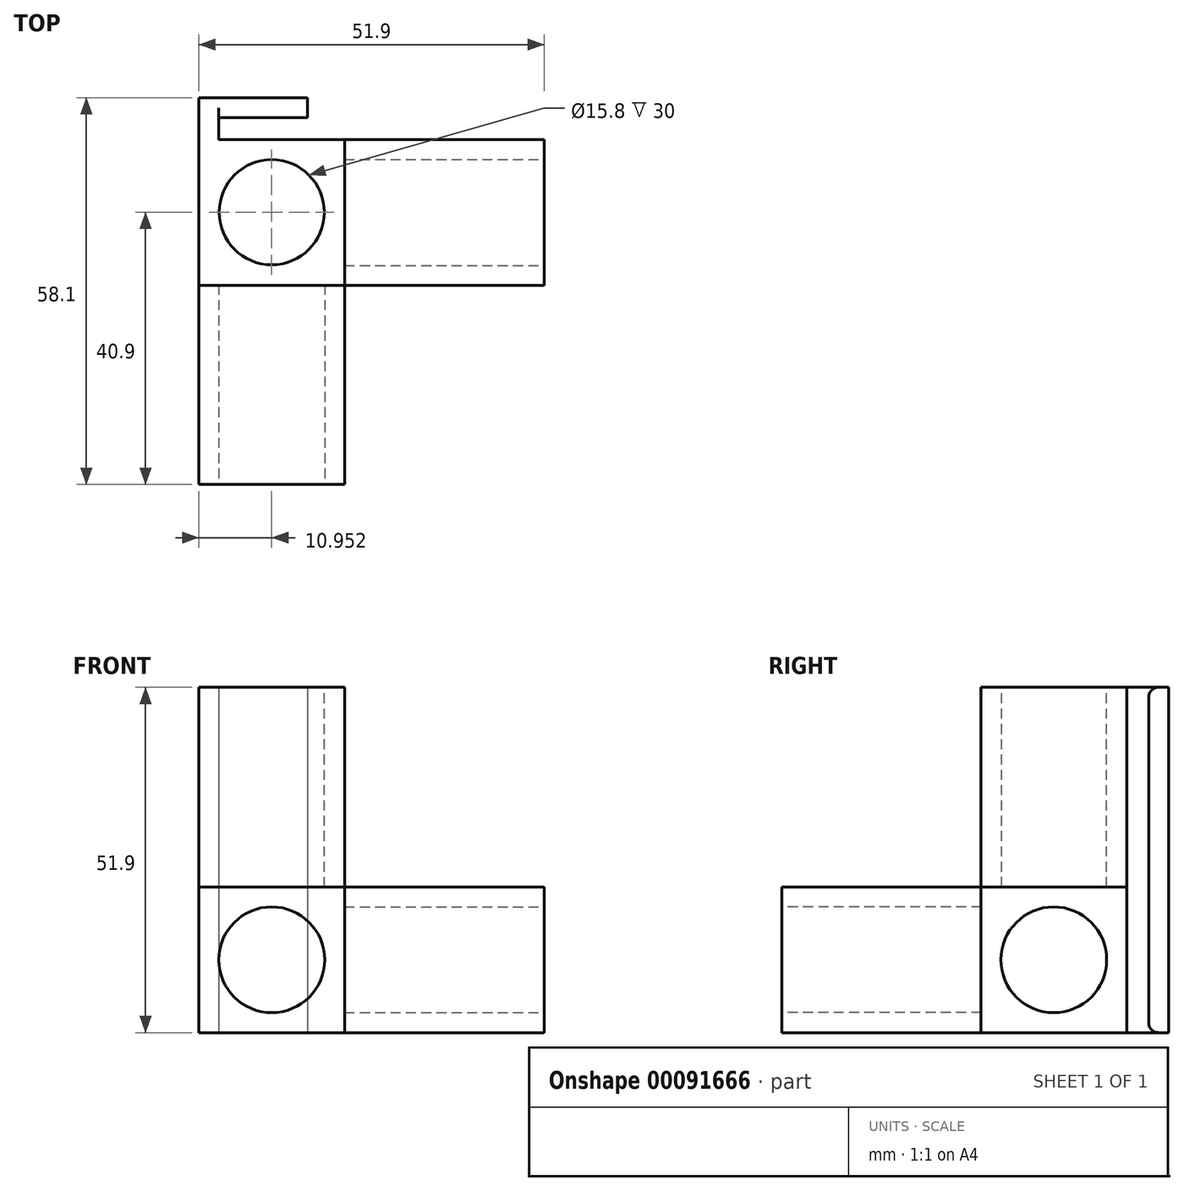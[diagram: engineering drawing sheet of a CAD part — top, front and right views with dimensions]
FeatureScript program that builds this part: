
annotation { "Feature Type Name" : "Feature", "Feature Type Description" : "" }
export const myFeature = defineFeature(function(context is Context, id is Id, definition is map)
    precondition{}
    {
        {
            var Q0;
            Q0=qCreatedBy(makeId("Front.planeOp"),FACE);
            var sketch = newSketch(context, id + "F0", { "sketchPlane" : qUnion([Q0])});
            skLineSegment(sketch, "E0.bottom", {"start": v(-42.3, 45.9) * mm, "end": v(-26.4, 45.9) * mm});
            skLineSegment(sketch, "E0.top", {"start": v(-42.3, 0) * mm, "end": v(-26.4, 0) * mm});
            skLineSegment(sketch, "E0.left", {"start": v(-42.3, 45.9) * mm, "end": v(-42.3, 0) * mm});
            skLineSegment(sketch, "E0.right", {"start": v(-26.4, 45.9) * mm, "end": v(-26.4, 15.9) * mm});
            skLineSegment(sketch, "E1.top", {"start": v(-42.3, 15.9) * mm, "end": v(-26.4, 15.9) * mm});
            skLineSegment(sketch, "E1.left", {"start": v(-42.3, 0) * mm, "end": v(-42.3, 15.9) * mm});
            skLineSegment(sketch, "E1.right", {"start": v(3.6, 0) * mm, "end": v(3.6, 15.9) * mm});
            skLineSegment(sketch, "E2", {"start": v(-26.4, 15.9) * mm, "end": v(-26.4, 0) * mm});
            skLineSegment(sketch, "E3", {"start": v(-26.4, 15.9) * mm, "end": v(3.6, 15.9) * mm});
            skLineSegment(sketch, "E4", {"start": v(-26.4, 0) * mm, "end": v(-26.4, 0) * mm});
            skLineSegment(sketch, "E5", {"start": v(-42.3, 15.9) * mm, "end": v(-42.3, 15.9) * mm});
            skLineSegment(sketch, "E6", {"start": v(-26.4, 0) * mm, "end": v(3.6, 0) * mm});
            skLineSegment(sketch, "E7.0", {"start": v(-45.3, 48.9) * mm, "end": v(-45.3, -3) * mm});
            skLineSegment(sketch, "E7.1", {"start": v(-45.3, -3) * mm, "end": v(-23.4, -3) * mm});
            skLineSegment(sketch, "E7.2", {"start": v(-23.4, 48.9) * mm, "end": v(-23.4, 18.9) * mm});
            skLineSegment(sketch, "E7.3", {"start": v(-23.4, 18.9) * mm, "end": v(6.6, 18.9) * mm});
            skLineSegment(sketch, "E7.4", {"start": v(6.6, -3) * mm, "end": v(6.6, 18.9) * mm});
            skLineSegment(sketch, "E7.5", {"start": v(-45.3, 48.9) * mm, "end": v(-23.4, 48.9) * mm});
            skLineSegment(sketch, "E7.6", {"start": v(-23.4, -3) * mm, "end": v(6.6, -3) * mm});
            skPoint(sketch, "E8", {"position": v(-34.36, 7.95) * mm});
            skPoint(sketch, "E8.positionSnap0", {"position": v(-26.4, 7.95) * mm});
            skPoint(sketch, "E8.positionSnap1", {"position": v(-34.36, 15.9) * mm});
            skCircle(sketch, "E9", {"center": v(-34.36, 7.95) * mm, "radius": 7.95 * mm});
            skLineSegment(sketch, "E10", {"start": v(-23.4, 18.9) * mm, "end": v(-45.3, 18.9) * mm});
            skLineSegment(sketch, "E11", {"start": v(-23.4, 18.9) * mm, "end": v(-23.4, -3) * mm});
            skSolve(sketch);
        }
        {
            var Q0;
            {var subQ1=sQuery(id+"F0.wireOp",EDGE,"E1.top");var subQ3=sQuery(id+"F0.wireOp",EDGE,"E9");var subQ4=makeQuery(id+"F0.imprint","INTERSECT",VERTEX,{"derivedFrom":[subQ1,subQ3]});Q0=makeQuery(id+"F0.imprint","IMPRINT",FACE,{"disambiguationData":[TD([[makeQuery(id+"F0.imprint","IMPRINT",EDGE,{"disambiguationData":[TD([[subQ4,-1.0]])],"derivedFrom":subQ3}),-1.0]])]});}
            var Q1;
            {var subQ0=sQuery(id+"F0.wireOp",EDGE,"E9");var subQ1=makeQuery(id+"F0.imprint","INTERSECT",VERTEX,{"derivedFrom":[sQuery(id+"F0.wireOp",EDGE,"E1.top"),subQ0]});Q1=makeQuery(id+"F0.imprint","IMPRINT",FACE,{"disambiguationData":[TD([[makeQuery(id+"F0.imprint","IMPRINT",EDGE,{"disambiguationData":[TD([[subQ1,1.0]])],"derivedFrom":subQ0}),1.0]])]});}
            var Q2;
            {var subQ5=sQuery(id+"F0.wireOp",EDGE,"E0.bottom");Q2=makeQuery(id+"F0.imprint","IMPRINT",FACE,{"disambiguationData":[TD([[makeQuery(id+"F0.imprint","IMPRINT",EDGE,{"derivedFrom":subQ5}),1.0]])]});}
            var Q3;
            {var subQ0=sQuery(id+"F0.wireOp",EDGE,"E1.right");Q3=makeQuery(id+"F0.imprint","IMPRINT",FACE,{"disambiguationData":[TD([[makeQuery(id+"F0.imprint","IMPRINT",EDGE,{"derivedFrom":subQ0}),1.0]])]});}
            var Q4;
            {var subQ0=sQuery(id+"F0.wireOp",EDGE,"E0.bottom");Q4=makeQuery(id+"F0.imprint","IMPRINT",FACE,{"disambiguationData":[TD([[makeQuery(id+"F0.imprint","IMPRINT",EDGE,{"derivedFrom":subQ0}),-1.0]])]});}
            var Q5;
            {var subQ0=sQuery(id+"F0.wireOp",EDGE,"E1.left");var subQ1=sQuery(id+"F0.wireOp",EDGE,"E0.top");var subQ2=makeQuery(id+"F0.imprint","INTERSECT",VERTEX,{"derivedFrom":[subQ1,subQ0]});Q5=makeQuery(id+"F0.imprint","IMPRINT",FACE,{"disambiguationData":[TD([[makeQuery(id+"F0.imprint","IMPRINT",EDGE,{"disambiguationData":[TD([[subQ2,-1.0]])],"derivedFrom":subQ1}),1.0]])]});}
            var Q6;
            {var subQ1=sQuery(id+"F0.wireOp",EDGE,"E0.top");var subQ3=sQuery(id+"F0.wireOp",EDGE,"E9");var subQ4=makeQuery(id+"F0.imprint","INTERSECT",VERTEX,{"derivedFrom":[subQ1,subQ3]});Q6=makeQuery(id+"F0.imprint","IMPRINT",FACE,{"disambiguationData":[TD([[makeQuery(id+"F0.imprint","IMPRINT",EDGE,{"disambiguationData":[TD([[subQ4,-1.0]])],"derivedFrom":subQ3}),-1.0]])]});}
            var Q7;
            {var subQ1=sQuery(id+"F0.wireOp",EDGE,"E1.top");var subQ3=sQuery(id+"F0.wireOp",EDGE,"E9");var subQ4=makeQuery(id+"F0.imprint","INTERSECT",VERTEX,{"derivedFrom":[subQ1,subQ3]});Q7=makeQuery(id+"F0.imprint","IMPRINT",FACE,{"disambiguationData":[TD([[makeQuery(id+"F0.imprint","IMPRINT",EDGE,{"disambiguationData":[TD([[subQ4,1.0]])],"derivedFrom":subQ3}),-1.0]])]});}
            var Q8;
            {var subQ5=sQuery(id+"F0.wireOp",EDGE,"E1.right");Q8=makeQuery(id+"F0.imprint","IMPRINT",FACE,{"disambiguationData":[TD([[makeQuery(id+"F0.imprint","IMPRINT",EDGE,{"derivedFrom":subQ5}),-1.0]])]});}
            var Q9;
            {var subQ4=sQuery(id+"F0.wireOp",EDGE,"E0.left");var subQ6=sQuery(id+"F0.wireOp",EDGE,"E10");var subQ8=makeQuery(id+"F0.imprint","INTERSECT",VERTEX,{"derivedFrom":[subQ4,subQ6]});Q9=makeQuery(id+"F0.imprint","IMPRINT",FACE,{"disambiguationData":[TD([[makeQuery(id+"F0.imprint","IMPRINT",EDGE,{"disambiguationData":[TD([[subQ8,1.0]])],"derivedFrom":subQ6}),1.0]])]});}
            var Q10;
            {var subQ3=sQuery(id+"F0.wireOp",EDGE,"E11");var subQ5=sQuery(id+"F0.wireOp",EDGE,"E3");var subQ8=makeQuery(id+"F0.imprint","INTERSECT",VERTEX,{"derivedFrom":[subQ5,subQ3]});Q10=makeQuery(id+"F0.imprint","IMPRINT",FACE,{"disambiguationData":[TD([[makeQuery(id+"F0.imprint","IMPRINT",EDGE,{"disambiguationData":[TD([[subQ8,-1.0]])],"derivedFrom":subQ3}),-1.0]])]});}
            var Q11;
            {var subQ14=sQuery(id+"F0.wireOp",EDGE,"E7.1");Q11=makeQuery(id+"F0.imprint","IMPRINT",FACE,{"disambiguationData":[TD([[makeQuery(id+"F0.imprint","IMPRINT",EDGE,{"derivedFrom":subQ14}),1.0]])]});}
            var Q12;
            {var subQ1=sQuery(id+"F0.wireOp",EDGE,"E0.right");var subQ3=sQuery(id+"F0.wireOp",EDGE,"E10");var subQ4=makeQuery(id+"F0.imprint","INTERSECT",VERTEX,{"derivedFrom":[subQ1,subQ3]});Q12=makeQuery(id+"F0.imprint","IMPRINT",FACE,{"disambiguationData":[TD([[makeQuery(id+"F0.imprint","IMPRINT",EDGE,{"disambiguationData":[TD([[subQ4,-1.0]])],"derivedFrom":subQ1}),1.0]])]});}
            extrude(context, id + "F1", {"entities" : qUnion([Q0, Q1, Q2, Q3, Q4, Q5, Q6, Q7, Q8, Q9, Q10, Q11, Q12]), "depth" : (15.9 + 6) * mm});
        }
        {
            var Q0;
            {var subQ14=sQuery(id+"F0.wireOp",EDGE,"E7.1");Q0=makeQuery(id+"F0.imprint","IMPRINT",FACE,{"disambiguationData":[TD([[makeQuery(id+"F0.imprint","IMPRINT",EDGE,{"derivedFrom":subQ14}),1.0]])]});}
            var Q1;
            {var subQ0=sQuery(id+"F0.wireOp",EDGE,"E9");var subQ1=makeQuery(id+"F0.imprint","INTERSECT",VERTEX,{"derivedFrom":[sQuery(id+"F0.wireOp",EDGE,"E1.top"),subQ0]});Q1=makeQuery(id+"F0.imprint","IMPRINT",FACE,{"disambiguationData":[TD([[makeQuery(id+"F0.imprint","IMPRINT",EDGE,{"disambiguationData":[TD([[subQ1,1.0]])],"derivedFrom":subQ0}),1.0]])]});}
            var Q2;
            {var subQ4=sQuery(id+"F0.wireOp",EDGE,"E0.left");var subQ6=sQuery(id+"F0.wireOp",EDGE,"E10");var subQ8=makeQuery(id+"F0.imprint","INTERSECT",VERTEX,{"derivedFrom":[subQ4,subQ6]});Q2=makeQuery(id+"F0.imprint","IMPRINT",FACE,{"disambiguationData":[TD([[makeQuery(id+"F0.imprint","IMPRINT",EDGE,{"disambiguationData":[TD([[subQ8,1.0]])],"derivedFrom":subQ6}),1.0]])]});}
            var Q3;
            {var subQ3=sQuery(id+"F0.wireOp",EDGE,"E11");var subQ5=sQuery(id+"F0.wireOp",EDGE,"E3");var subQ8=makeQuery(id+"F0.imprint","INTERSECT",VERTEX,{"derivedFrom":[subQ5,subQ3]});Q3=makeQuery(id+"F0.imprint","IMPRINT",FACE,{"disambiguationData":[TD([[makeQuery(id+"F0.imprint","IMPRINT",EDGE,{"disambiguationData":[TD([[subQ8,-1.0]])],"derivedFrom":subQ3}),-1.0]])]});}
            var Q4;
            {var subQ1=sQuery(id+"F0.wireOp",EDGE,"E0.right");var subQ3=sQuery(id+"F0.wireOp",EDGE,"E10");var subQ4=makeQuery(id+"F0.imprint","INTERSECT",VERTEX,{"derivedFrom":[subQ1,subQ3]});Q4=makeQuery(id+"F0.imprint","IMPRINT",FACE,{"disambiguationData":[TD([[makeQuery(id+"F0.imprint","IMPRINT",EDGE,{"disambiguationData":[TD([[subQ4,-1.0]])],"derivedFrom":subQ1}),1.0]])]});}
            var Q5;
            {var subQ1=sQuery(id+"F0.wireOp",EDGE,"E1.top");var subQ3=sQuery(id+"F0.wireOp",EDGE,"E9");var subQ4=makeQuery(id+"F0.imprint","INTERSECT",VERTEX,{"derivedFrom":[subQ1,subQ3]});Q5=makeQuery(id+"F0.imprint","IMPRINT",FACE,{"disambiguationData":[TD([[makeQuery(id+"F0.imprint","IMPRINT",EDGE,{"disambiguationData":[TD([[subQ4,1.0]])],"derivedFrom":subQ3}),-1.0]])]});}
            var Q6;
            {var subQ1=sQuery(id+"F0.wireOp",EDGE,"E1.top");var subQ3=sQuery(id+"F0.wireOp",EDGE,"E9");var subQ4=makeQuery(id+"F0.imprint","INTERSECT",VERTEX,{"derivedFrom":[subQ1,subQ3]});Q6=makeQuery(id+"F0.imprint","IMPRINT",FACE,{"disambiguationData":[TD([[makeQuery(id+"F0.imprint","IMPRINT",EDGE,{"disambiguationData":[TD([[subQ4,-1.0]])],"derivedFrom":subQ3}),-1.0]])]});}
            var Q7;
            {var subQ0=sQuery(id+"F0.wireOp",EDGE,"E1.left");var subQ1=sQuery(id+"F0.wireOp",EDGE,"E0.top");var subQ2=makeQuery(id+"F0.imprint","INTERSECT",VERTEX,{"derivedFrom":[subQ1,subQ0]});Q7=makeQuery(id+"F0.imprint","IMPRINT",FACE,{"disambiguationData":[TD([[makeQuery(id+"F0.imprint","IMPRINT",EDGE,{"disambiguationData":[TD([[subQ2,-1.0]])],"derivedFrom":subQ1}),1.0]])]});}
            var Q8;
            {var subQ1=sQuery(id+"F0.wireOp",EDGE,"E0.top");var subQ3=sQuery(id+"F0.wireOp",EDGE,"E9");var subQ4=makeQuery(id+"F0.imprint","INTERSECT",VERTEX,{"derivedFrom":[subQ1,subQ3]});Q8=makeQuery(id+"F0.imprint","IMPRINT",FACE,{"disambiguationData":[TD([[makeQuery(id+"F0.imprint","IMPRINT",EDGE,{"disambiguationData":[TD([[subQ4,-1.0]])],"derivedFrom":subQ3}),-1.0]])]});}
            extrude(context, id + "F2", {"entities" : qUnion([Q0, Q1, Q2, Q3, Q4, Q5, Q6, Q7, Q8]), "operationType" : NewBodyOperationType.ADD, "depth" : (15.8 + 6 + 30) * mm});
        }
        {
            var Q0;
            Q0=makeQuery(id+"F2.opExtrude","CAP_FACE",FACE,{"disambiguationData":[OSD([sQuery(id+"F0.wireOp",EDGE,"E7.0"),sQuery(id+"F0.wireOp",EDGE,"E7.1"),sQuery(id+"F0.wireOp",EDGE,"E10"),sQuery(id+"F0.wireOp",EDGE,"E11")])],"isStart":false});
            var sketch = newSketch(context, id + "F3", { "sketchPlane" : qUnion([Q0])});
            skCircle(sketch, "E12.0", {"center": v(-34.36, 7.95) * mm, "radius": 7.95 * mm});
            skSolve(sketch);
        }
        {
            var Q0;
            Q0=makeQuery(id+"F1.opExtrude","SWEPT_FACE",FACE,{"disambiguationData":[OSD([sQuery(id+"F0.wireOp",EDGE,"E7.5")])]});
            var sketch = newSketch(context, id + "F4", { "sketchPlane" : qUnion([Q0])});
            skPoint(sketch, "E13", {"position": v(-34.36, -3) * mm});
            skPoint(sketch, "E14", {"position": v(-26.4, -10.9) * mm});
            skPoint(sketch, "E15", {"position": v(-34.36, -10.9) * mm});
            skPoint(sketch, "E16", {"position": v(-62.98, 75) * mm});
            skPoint(sketch, "E17.orphan", {"position": v(-42.3, -3) * mm});
            skPoint(sketch, "E18.orphan", {"position": v(-26.4, -3) * mm});
            skPoint(sketch, "E19.orphan", {"position": v(-26.4, -18.8) * mm});
            skCircle(sketch, "E20", {"center": v(-34.36, -10.9) * mm, "radius": 7.9 * mm});
            skSolve(sketch);
        }
        {
            var Q0;
            Q0=makeQuery(id+"F1.opExtrude","SWEPT_FACE",FACE,{"disambiguationData":[OSD([sQuery(id+"F0.wireOp",EDGE,"E7.4")])]});
            var sketch = newSketch(context, id + "F5", { "sketchPlane" : qUnion([Q0])});
            skLineSegment(sketch, "E21.0", {"start": v(-18.9, 15.9) * mm, "end": v(-3, 15.9) * mm});
            skLineSegment(sketch, "E21.1", {"start": v(-18.9, 0) * mm, "end": v(-18.9, 15.9) * mm});
            skLineSegment(sketch, "E21.2", {"start": v(-18.9, 0) * mm, "end": v(-3, 0) * mm});
            skLineSegment(sketch, "E21.3", {"start": v(-3, 0) * mm, "end": v(-3, 15.9) * mm});
            skCircle(sketch, "E22", {"center": v(-10.95, 7.95) * mm, "radius": 7.95 * mm});
            skPoint(sketch, "E22.centerSnap0", {"position": v(-10.95, 0) * mm});
            skPoint(sketch, "E22.centerSnap1", {"position": v(-3, 7.95) * mm});
            skSolve(sketch);
        }
        {
            var Q0;
            Q0=makeQuery(id+"F3.imprint","IMPRINT",FACE,{"disambiguationData":[TD([[makeQuery(id+"F3.imprint","IMPRINT",EDGE,{"derivedFrom":sQuery(id+"F3.wireOp",EDGE,"E12.0")}),1.0]])]});
            extrude(context, id + "F6", {"entities" : qUnion([Q0]), "operationType" : NewBodyOperationType.REMOVE, "oppositeDirection" : true, "depth" : 30 * mm});
        }
        {
            var Q0;
            {var subQ0=sQuery(id+"F5.wireOp",EDGE,"E22");var subQ1=makeQuery(id+"F5.imprint","INTERSECT",VERTEX,{"derivedFrom":[sQuery(id+"F5.wireOp",EDGE,"E21.1"),subQ0]});Q0=makeQuery(id+"F5.imprint","IMPRINT",FACE,{"disambiguationData":[TD([[makeQuery(id+"F5.imprint","IMPRINT",EDGE,{"disambiguationData":[TD([[subQ1,1.0]])],"derivedFrom":subQ0}),1.0]])]});}
            extrude(context, id + "F7", {"entities" : qUnion([Q0]), "operationType" : NewBodyOperationType.REMOVE, "oppositeDirection" : true, "depth" : 30 * mm});
        }
        {
            var Q0;
            Q0=makeQuery(id+"F4.imprint","IMPRINT",FACE,{"disambiguationData":[TD([[makeQuery(id+"F4.imprint","IMPRINT",EDGE,{"derivedFrom":sQuery(id+"F4.wireOp",EDGE,"E20")}),1.0]])]});
            var Q1;
            Q1=sQuery(id+"F4.wireOp",EDGE,"E20");
            extrude(context, id + "F8", {"entities" : qUnion([Q0]), "operationType" : NewBodyOperationType.REMOVE, "surfaceEntities" : qUnion([Q1]), "oppositeDirection" : true, "depth" : 30 * mm});
        }
        {
            var Q0;
            {var subQ0=sQuery(id+"F0.wireOp",EDGE,"E7.1");Q0=makeQuery(id+"F2.boolean.opBoolean","MERGE",FACE,{"derivedFrom":[makeQuery(id+"F1.opExtrude","SWEPT_FACE",FACE,{"disambiguationData":[OSD([subQ0,sQuery(id+"F0.wireOp",EDGE,"E7.6")])]}),makeQuery(id+"F2.opExtrude","SWEPT_FACE",FACE,{"disambiguationData":[OSD([subQ0])]})]});}
            var sketch = newSketch(context, id + "F9", { "sketchPlane" : qUnion([Q0])});
            skLineSegment(sketch, "E23", {"start": v(-45.3, 0) * mm, "end": v(-45.3, -6.3) * mm});
            skLineSegment(sketch, "E24", {"start": v(-45.3, -6.3) * mm, "end": v(-29, -6.3) * mm});
            skLineSegment(sketch, "E25", {"start": v(-29, -6.3) * mm, "end": v(-29, -3.3) * mm});
            skLineSegment(sketch, "E26", {"start": v(-29, -3.3) * mm, "end": v(-42.3, -3.3) * mm});
            skLineSegment(sketch, "E27", {"start": v(-42.3, -3.3) * mm, "end": v(-42.3, 0) * mm});
            skSolve(sketch);
        }
        {
            var Q0;
            Q0 = qSketchRegion(id + "F9", true);
            var Q1;
            {var subQ0=sQuery(id+"F9.wireOp",EDGE,"E23");Q1=makeQuery(id+"F9.imprint","IMPRINT",FACE,{"disambiguationData":[TD([[makeQuery(id+"F9.imprint","IMPRINT",EDGE,{"derivedFrom":subQ0}),1.0]])]});}
            extrude(context, id + "F10", {"entities" : qUnion([Q0, Q1]), "operationType" : NewBodyOperationType.ADD, "oppositeDirection" : true, "depth" : (6 + 15.9 + 30) * mm});
        }
        {
            var Q0;
            Q0=makeQuery(id+"F10.opExtrude","CAP_EDGE",EDGE,{"disambiguationData":[OSD([sQuery(id+"F9.wireOp",EDGE,"E26")])],"isStart":true});
            var Q1;
            Q1=makeQuery(id+"F10.opExtrude","CAP_EDGE",EDGE,{"disambiguationData":[OSD([sQuery(id+"F9.wireOp",EDGE,"E26")])],"isStart":false});
            fillet(context, id + "F11", {"entities" : qUnion([Q0, Q1]), "radius" : 1.5 * mm, "tangentPropagation" : true, "allowEdgeOverflow" : false});
        }
    });
